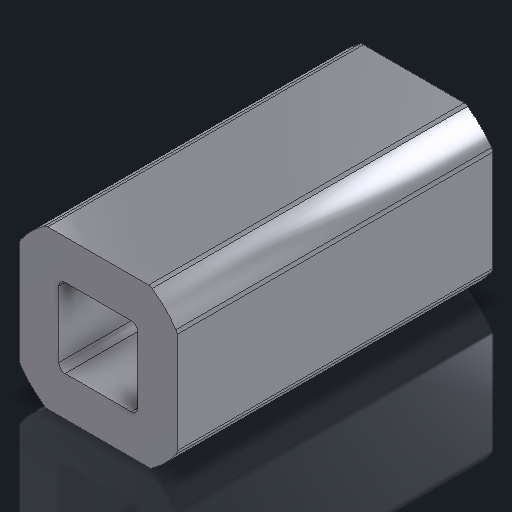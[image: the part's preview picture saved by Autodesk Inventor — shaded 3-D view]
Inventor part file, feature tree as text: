
AUTODESK INVENTOR PART (.ipt)
format: ipt  version: 2023.2 (Build 272271030, 271C)  size: 172,032 bytes
history: native  units: in
note: dims shown in document units (in); Inventor stores cm internally (conversion verified against a paired STEP export)
features: other x3, sketch x2
ambient origin geometry x8: Origin, YZ Plane, XZ Plane, XY Plane, X Axis, Y Axis, Z Axis, Center Point
bodies: Solid1 (feature_tree)
feature tree (5):
  other  "HS Shaft Adapter Square.ipt"
  other  "Solid1::HS Shaft Adapter Square.ipt"
  other  "TaggingFeature1"
  sketch  "Sketch1"  dims[d0=0.3937in]
  sketch  "Sketch2"
